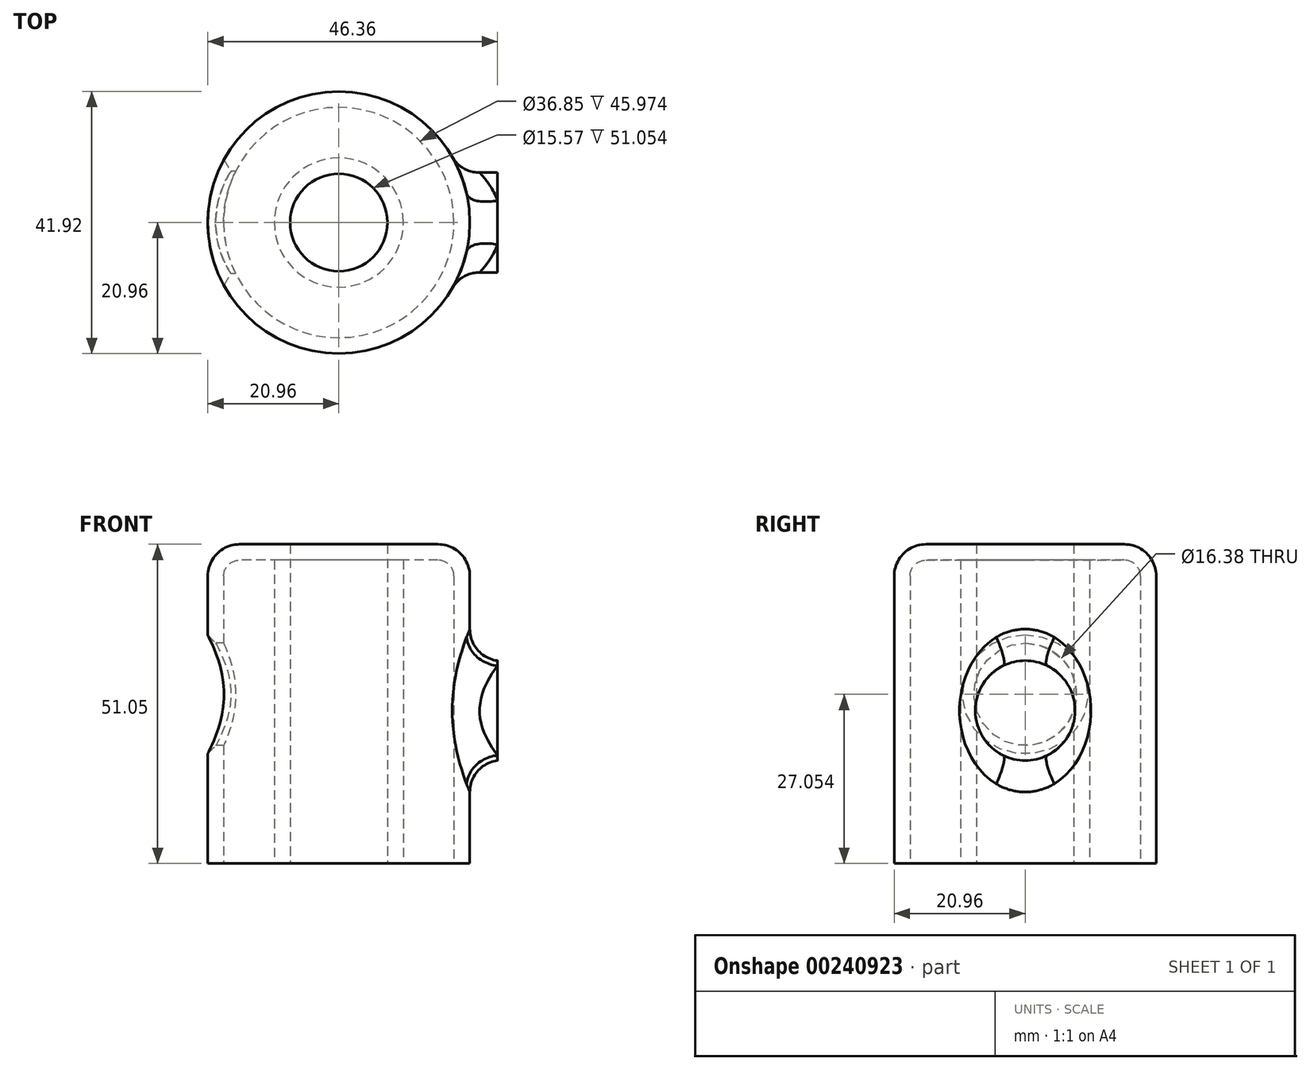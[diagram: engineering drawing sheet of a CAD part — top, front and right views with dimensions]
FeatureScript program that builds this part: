
annotation { "Feature Type Name" : "Feature", "Feature Type Description" : "" }
export const myFeature = defineFeature(function(context is Context, id is Id, definition is map)
    precondition{}
    {
        {
            var Q0;
            Q0=qCreatedBy(makeId("Top.planeOp"),FACE);
            var sketch = newSketch(context, id + "F0", { "sketchPlane" : qUnion([Q0])});
            skCircle(sketch, "E0", {"center": v(0, 0) * mm, "radius": 20.96 * mm});
            skCircle(sketch, "E1", {"center": v(0, 0) * mm, "radius": 7.79 * mm});
            skSolve(sketch);
        }
        {
            var Q0;
            Q0=makeQuery(id+"F0.imprint","IMPRINT",FACE,{"disambiguationData":[TD([[makeQuery(id+"F0.imprint","IMPRINT",EDGE,{"derivedFrom":sQuery(id+"F0.wireOp",EDGE,"E0")}),1.0]])]});
            extrude(context, id + "F1", {"entities" : qUnion([Q0]), "depth" : 51.05 * mm});
        }
        {
            var Q0;
            Q0=makeQuery(id+"F1.opExtrude","CAP_EDGE",EDGE,{"disambiguationData":[OSD([sQuery(id+"F0.wireOp",EDGE,"E0")])],"isStart":false});
            fillet(context, id + "F2", {"entities" : qUnion([Q0]), "radius" : 5.08 * mm, "tangentPropagation" : true, "allowEdgeOverflow" : false});
        }
        {
            var Q0;
            Q0=makeQuery(id+"F1.opExtrude","CAP_FACE",FACE,{"disambiguationData":[OSD([sQuery(id+"F0.wireOp",EDGE,"E0"),sQuery(id+"F0.wireOp",EDGE,"E1")])],"isStart":true});
            shell(context, id + "F3", {"entities" : qUnion([Q0]), "thickness" : 2.54 * mm});
        }
        {
            var Q0;
            Q0=qCreatedBy(makeId("Right.planeOp"),FACE);
            cPlane(context, id + "F4", {"entities" : qUnion([Q0]), "cplaneType" : CPlaneType.OFFSET, "offset" : 25.4 * mm, "oppositeDirection" : true, "width" : 152.4 * mm, "height" : 152.4 * mm});
        }
        {
            var Q0;
            Q0=qCreatedBy(id+"F4.planeOp",FACE);
            var sketch = newSketch(context, id + "F5", { "sketchPlane" : qUnion([Q0])});
            skCircle(sketch, "E2", {"center": v(0, 27.05) * mm, "radius": 8.2 * mm});
            skSolve(sketch);
        }
        {
            var Q0;
            Q0=makeQuery(id+"F5.imprint","IMPRINT",FACE,{"disambiguationData":[TD([[makeQuery(id+"F5.imprint","IMPRINT",EDGE,{"derivedFrom":sQuery(id+"F5.wireOp",EDGE,"E2")}),1.0]])]});
            extrude(context, id + "F6", {"entities" : qUnion([Q0]), "operationType" : NewBodyOperationType.REMOVE, "depth" : 11.94 * mm});
        }
        {
            var Q0;
            Q0=makeQuery(id+"F6.boolean.opBoolean","INTERSECT",EDGE,{"derivedFrom":[makeQuery(id+"F1.opExtrude","SWEPT_FACE",FACE,{"disambiguationData":[OSD([sQuery(id+"F0.wireOp",EDGE,"E0")])]}),makeQuery(id+"F6.opExtrude","SWEPT_FACE",FACE,{"disambiguationData":[OSD([sQuery(id+"F5.wireOp",EDGE,"E2")])]})]});
            chamfer(context, id + "F7", {"entities" : qUnion([Q0]), "width" : 1.27 * mm, "tangentPropagation" : true});
        }
        {
            var Q0;
            Q0=qCreatedBy(makeId("Right.planeOp"),FACE);
            cPlane(context, id + "F8", {"entities" : qUnion([Q0]), "cplaneType" : CPlaneType.OFFSET, "offset" : 25.4 * mm, "width" : 152.4 * mm, "height" : 152.4 * mm});
        }
        {
            var Q0;
            Q0=qCreatedBy(id+"F8.planeOp",FACE);
            var sketch = newSketch(context, id + "F9", { "sketchPlane" : qUnion([Q0])});
            skCircle(sketch, "E3", {"center": v(0, 24.46) * mm, "radius": 7.98 * mm});
            skSolve(sketch);
        }
        {
            var Q0;
            Q0=makeQuery(id+"F9.imprint","IMPRINT",FACE,{"disambiguationData":[TD([[makeQuery(id+"F9.imprint","IMPRINT",EDGE,{"derivedFrom":sQuery(id+"F9.wireOp",EDGE,"E3")}),1.0]])]});
            extrude(context, id + "F10", {"entities" : qUnion([Q0]), "operationType" : NewBodyOperationType.ADD, "oppositeDirection" : true, "depth" : 6.35 * mm});
        }
        {
            var Q0;
            Q0=makeQuery(id+"F10.boolean.opBoolean","INTERSECT",EDGE,{"derivedFrom":[makeQuery(id+"F1.opExtrude","SWEPT_FACE",FACE,{"disambiguationData":[OSD([sQuery(id+"F0.wireOp",EDGE,"E0")])]}),makeQuery(id+"F10.opExtrude","SWEPT_FACE",FACE,{"disambiguationData":[OSD([sQuery(id+"F9.wireOp",EDGE,"E3")])]})]});
            fillet(context, id + "F11", {"entities" : qUnion([Q0]), "radius" : 5.08 * mm, "tangentPropagation" : true, "allowEdgeOverflow" : false});
        }
    });
